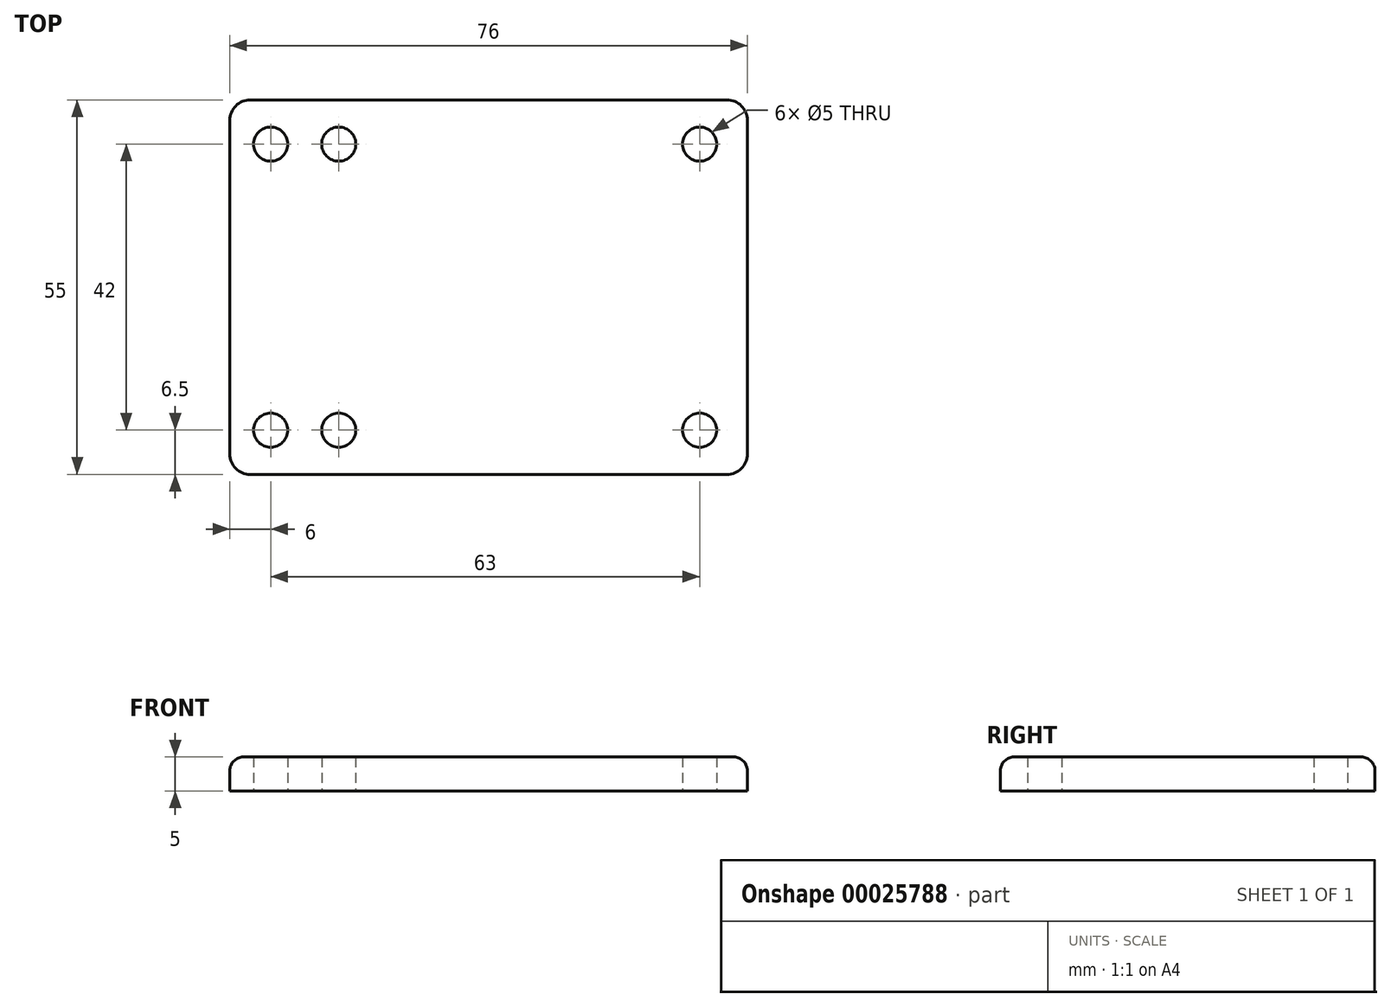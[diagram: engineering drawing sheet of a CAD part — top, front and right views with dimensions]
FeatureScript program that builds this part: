
annotation { "Feature Type Name" : "Feature", "Feature Type Description" : "" }
export const myFeature = defineFeature(function(context is Context, id is Id, definition is map)
    precondition{}
    {
        {
            var Q0;
            Q0=qCreatedBy(makeId("Top.planeOp"),FACE);
            var sketch = newSketch(context, id + "F0", { "sketchPlane" : qUnion([Q0])});
            skLineSegment(sketch, "E0.bottom", {"start": v(-25, -27.5) * mm, "end": v(45, -27.5) * mm});
            skLineSegment(sketch, "E0.top", {"start": v(-25, 27.5) * mm, "end": v(45, 27.5) * mm});
            skLineSegment(sketch, "E0.left", {"start": v(-28, -24.5) * mm, "end": v(-28, 24.5) * mm});
            skLineSegment(sketch, "E0.right", {"start": v(48, -24.5) * mm, "end": v(48, 24.5) * mm});
            skPoint(sketch, "E1", {"position": v(0, 0) * mm});
            skLineSegment(sketch, "E2", {"start": v(-28, 0) * mm, "end": v(48, 0) * mm, "construction": true});
            skLineSegment(sketch, "E3", {"start": v(-22, 27.5) * mm, "end": v(-22, -27.5) * mm, "construction": true});
            skLineSegment(sketch, "E4.0", {"start": v(-12, 27.5) * mm, "end": v(-12, -27.5) * mm, "construction": true});
            skLineSegment(sketch, "E5.0", {"start": v(41, 27.5) * mm, "end": v(41, -27.5) * mm, "construction": true});
            skLineSegment(sketch, "E6.0", {"start": v(-28, -21) * mm, "end": v(48, -21) * mm, "construction": true});
            skLineSegment(sketch, "E7.0", {"start": v(-28, 21) * mm, "end": v(48, 21) * mm, "construction": true});
            skCircle(sketch, "E8", {"center": v(-22, 21) * mm, "radius": 2.5 * mm});
            skCircle(sketch, "E9", {"center": v(-12, 21) * mm, "radius": 2.5 * mm});
            skCircle(sketch, "E10", {"center": v(41, 21) * mm, "radius": 2.5 * mm});
            skCircle(sketch, "E11", {"center": v(41, -21) * mm, "radius": 2.5 * mm});
            skCircle(sketch, "E12", {"center": v(-12, -21) * mm, "radius": 2.5 * mm});
            skCircle(sketch, "E13", {"center": v(-22, -21) * mm, "radius": 2.5 * mm});
            skLineSegment(sketch, "E14.rect.bottom", {"start": v(33, 9) * mm, "end": v(29, 9) * mm});
            skLineSegment(sketch, "E14.rect.top", {"start": v(33, -9) * mm, "end": v(29, -9) * mm});
            skLineSegment(sketch, "E14.rect.left", {"start": v(42, 0) * mm, "end": v(42, 0) * mm});
            skLineSegment(sketch, "E14.rect.right", {"start": v(20, 0) * mm, "end": v(20, 0) * mm});
            skPoint(sketch, "E14.rect.middle", {"position": v(31, 0) * mm});
            skPoint(sketch, "E15.visualSharp", {"position": v(20, 9) * mm});
            skArc(sketch, "E15.filletArc", {"start": v(29, 9) * mm, "mid": v(22.64, 6.36) * mm, "end": v(20, 0) * mm});
            skPoint(sketch, "E16.visualSharp", {"position": v(42, 9) * mm});
            skArc(sketch, "E16.filletArc", {"start": v(42, 0) * mm, "mid": v(39.36, 6.36) * mm, "end": v(33, 9) * mm});
            skPoint(sketch, "E17.visualSharp", {"position": v(42, -9) * mm});
            skArc(sketch, "E17.filletArc", {"start": v(33, -9) * mm, "mid": v(39.36, -6.36) * mm, "end": v(42, 0) * mm});
            skPoint(sketch, "E18.visualSharp", {"position": v(20, -9) * mm});
            skArc(sketch, "E18.filletArc", {"start": v(20, 0) * mm, "mid": v(22.64, -6.36) * mm, "end": v(29, -9) * mm});
            skPoint(sketch, "E19.visualSharp", {"position": v(48, 27.5) * mm});
            skArc(sketch, "E19.filletArc", {"start": v(48, 24.5) * mm, "mid": v(47.12, 26.62) * mm, "end": v(45, 27.5) * mm});
            skPoint(sketch, "E20.visualSharp", {"position": v(48, -27.5) * mm});
            skArc(sketch, "E20.filletArc", {"start": v(45, -27.5) * mm, "mid": v(47.12, -26.62) * mm, "end": v(48, -24.5) * mm});
            skPoint(sketch, "E21.visualSharp", {"position": v(-28, -27.5) * mm});
            skArc(sketch, "E21.filletArc", {"start": v(-28, -24.5) * mm, "mid": v(-27.12, -26.62) * mm, "end": v(-25, -27.5) * mm});
            skPoint(sketch, "E22.visualSharp", {"position": v(-28, 27.5) * mm});
            skArc(sketch, "E22.filletArc", {"start": v(-25, 27.5) * mm, "mid": v(-27.12, 26.62) * mm, "end": v(-28, 24.5) * mm});
            skSolve(sketch);
        }
        {
            var Q0;
            Q0=makeQuery(id+"F0.imprint","IMPRINT",FACE,{"disambiguationData":[TD([[makeQuery(id+"F0.imprint","IMPRINT",EDGE,{"derivedFrom":sQuery(id+"F0.wireOp",EDGE,"E0.bottom")}),1.0]])]});
            var Q1;
            Q1=makeQuery(id+"F0.imprint","IMPRINT",FACE,{"disambiguationData":[TD([[makeQuery(id+"F0.imprint","IMPRINT",EDGE,{"derivedFrom":sQuery(id+"F0.wireOp",EDGE,"E14.rect.bottom")}),1.0]])]});
            extrude(context, id + "F1", {"entities" : qUnion([Q0, Q1]), "depth" : 5 * mm});
        }
        {
            var Q0;
            Q0=makeQuery(id+"F1.opExtrude","CAP_EDGE",EDGE,{"disambiguationData":[OSD([sQuery(id+"F0.wireOp",EDGE,"E19.filletArc")])],"isStart":false});
            var Q1;
            Q1=makeQuery(id+"F1.opExtrude","CAP_EDGE",EDGE,{"disambiguationData":[OSD([sQuery(id+"F0.wireOp",EDGE,"E0.right")])],"isStart":false});
            var Q2;
            Q2=makeQuery(id+"F1.opExtrude","CAP_EDGE",EDGE,{"disambiguationData":[OSD([sQuery(id+"F0.wireOp",EDGE,"E20.filletArc")])],"isStart":false});
            var Q3;
            Q3=makeQuery(id+"F1.opExtrude","CAP_EDGE",EDGE,{"disambiguationData":[OSD([sQuery(id+"F0.wireOp",EDGE,"E0.bottom")])],"isStart":false});
            var Q4;
            Q4=makeQuery(id+"F1.opExtrude","CAP_EDGE",EDGE,{"disambiguationData":[OSD([sQuery(id+"F0.wireOp",EDGE,"E21.filletArc")])],"isStart":false});
            var Q5;
            Q5=makeQuery(id+"F1.opExtrude","CAP_EDGE",EDGE,{"disambiguationData":[OSD([sQuery(id+"F0.wireOp",EDGE,"E0.left")])],"isStart":false});
            var Q6;
            Q6=makeQuery(id+"F1.opExtrude","CAP_EDGE",EDGE,{"disambiguationData":[OSD([sQuery(id+"F0.wireOp",EDGE,"E22.filletArc")])],"isStart":false});
            var Q7;
            Q7=makeQuery(id+"F1.opExtrude","CAP_EDGE",EDGE,{"disambiguationData":[OSD([sQuery(id+"F0.wireOp",EDGE,"E0.top")])],"isStart":false});
            fillet(context, id + "F2", {"entities" : qUnion([Q0, Q1, Q2, Q3, Q4, Q5, Q6, Q7]), "radius" : 2 * mm, "tangentPropagation" : true, "allowEdgeOverflow" : false});
        }
    });
